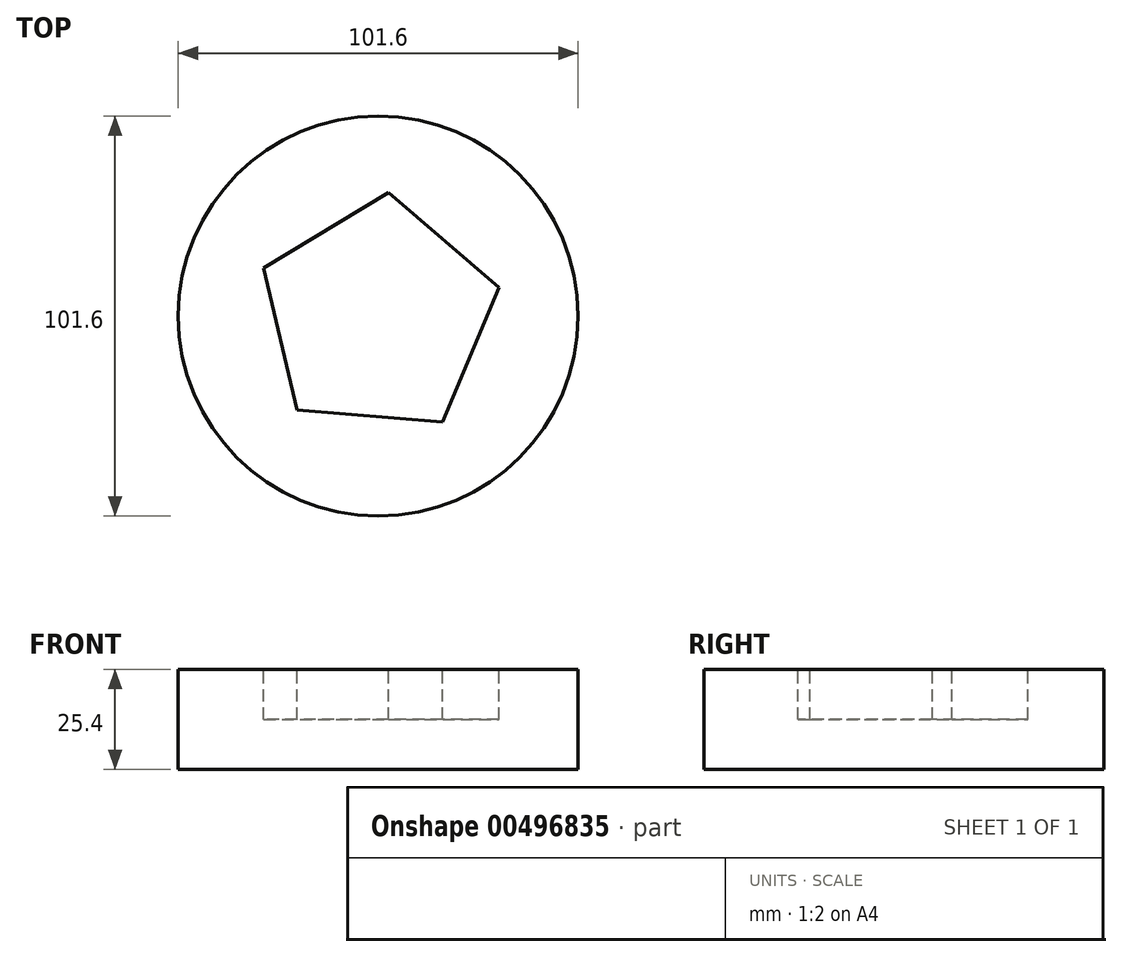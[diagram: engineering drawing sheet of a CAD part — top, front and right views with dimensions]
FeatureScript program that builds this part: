
annotation { "Feature Type Name" : "Feature", "Feature Type Description" : "" }
export const myFeature = defineFeature(function(context is Context, id is Id, definition is map)
    precondition{}
    {
        {
            var Q0;
            Q0=qCreatedBy(makeId("Top.planeOp"),FACE);
            var sketch = newSketch(context, id + "F0", { "sketchPlane" : qUnion([Q0])});
            skCircle(sketch, "E0", {"center": v(0, 0) * mm, "radius": 50.8 * mm});
            skSolve(sketch);
        }
        {
            var Q0;
            Q0 = qSketchRegion(id + "F0", true);
            extrude(context, id + "F1", {"entities" : qUnion([Q0]), "depth" : 25.4 * mm});
        }
        {
            var Q0;
            Q0=makeQuery(id+"F1.opExtrude","CAP_FACE",FACE,{"disambiguationData":[OSD([sQuery(id+"F0.wireOp",EDGE,"E0")])],"isStart":false});
            var sketch = newSketch(context, id + "F2", { "sketchPlane" : qUnion([Q0])});
            skCircle(sketch, "E1.cCircle", {"center": v(0, 0) * mm, "radius": 25.5 * mm, "construction": true});
            skLineSegment(sketch, "E1.0", {"start": v(2.63, 31.4) * mm, "end": v(30.68, 7.2) * mm});
            skLineSegment(sketch, "E1.1", {"start": v(30.68, 7.2) * mm, "end": v(16.33, -26.95) * mm});
            skLineSegment(sketch, "E1.2", {"start": v(16.33, -26.95) * mm, "end": v(-20.59, -23.86) * mm});
            skLineSegment(sketch, "E1.3", {"start": v(-20.59, -23.86) * mm, "end": v(-29.06, 12.2) * mm});
            skLineSegment(sketch, "E1.4", {"start": v(-29.06, 12.2) * mm, "end": v(2.63, 31.4) * mm});
            skPoint(sketch, "E1.0.midPoint", {"position": v(16.66, 19.3) * mm});
            skSolve(sketch);
        }
        {
            var Q0;
            Q0 = qSketchRegion(id + "F2", true);
            extrude(context, id + "F3", {"entities" : qUnion([Q0]), "operationType" : NewBodyOperationType.REMOVE, "oppositeDirection" : true, "depth" : 12.7 * mm});
        }
    });
